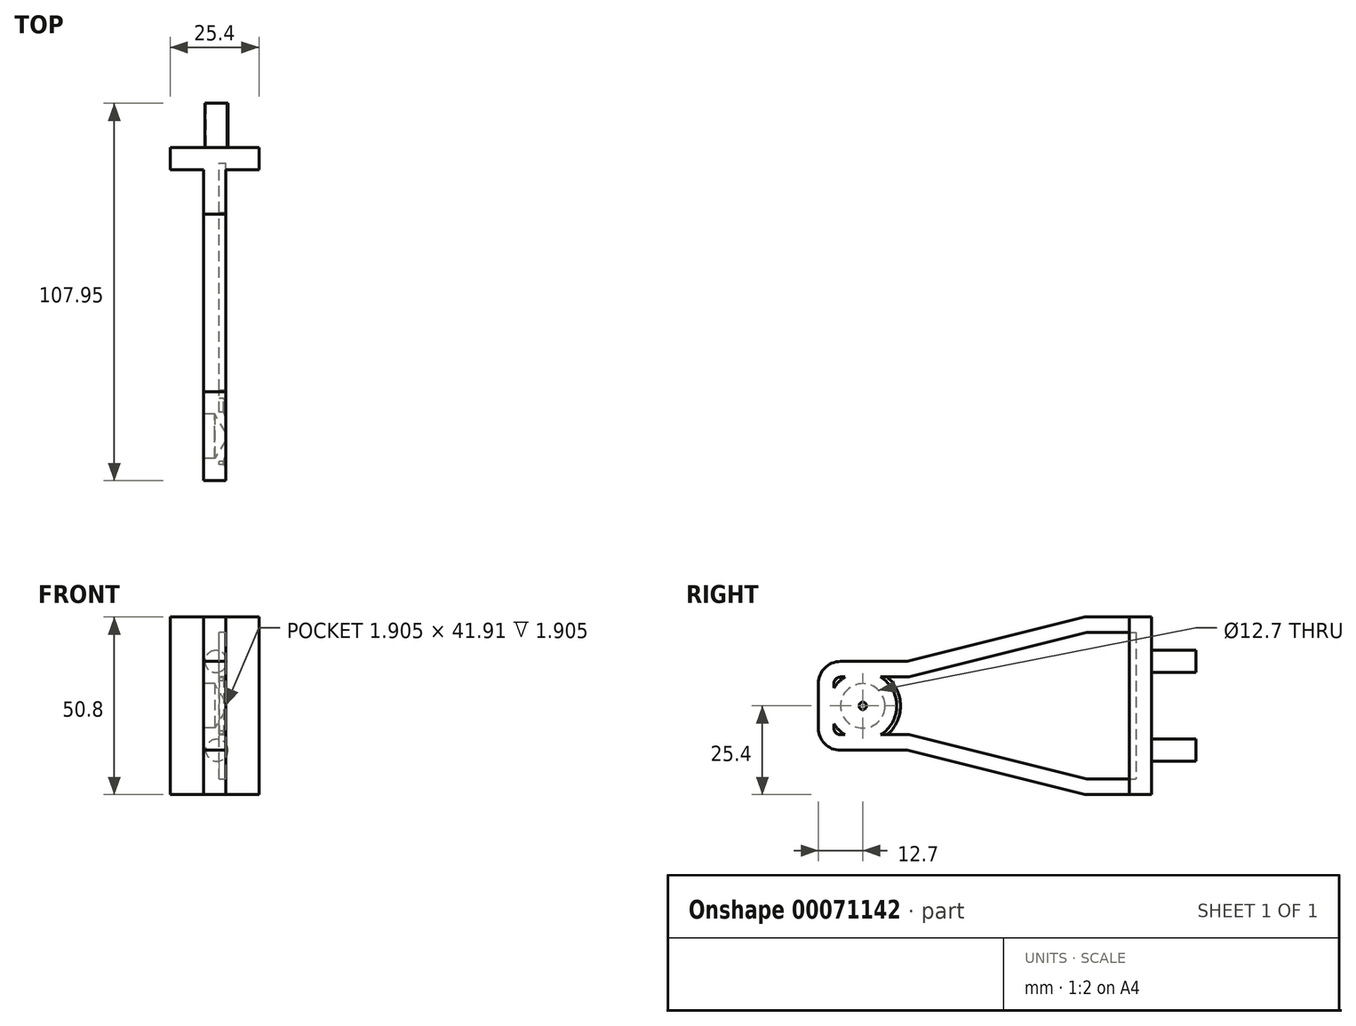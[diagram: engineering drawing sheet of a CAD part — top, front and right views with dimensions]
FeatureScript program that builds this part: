
annotation { "Feature Type Name" : "Feature", "Feature Type Description" : "" }
export const myFeature = defineFeature(function(context is Context, id is Id, definition is map)
    precondition{}
    {
        {
            var Q0;
            Q0=qCreatedBy(makeId("Front.planeOp"),FACE);
            var sketch = newSketch(context, id + "F0", { "sketchPlane" : qUnion([Q0])});
            skLineSegment(sketch, "E0.bottom", {"start": v(0, 0) * mm, "end": v(25.4, 0) * mm});
            skLineSegment(sketch, "E0.top", {"start": v(0, 50.8) * mm, "end": v(25.4, 50.8) * mm});
            skLineSegment(sketch, "E0.left", {"start": v(0, 0) * mm, "end": v(0, 50.8) * mm});
            skLineSegment(sketch, "E0.right", {"start": v(25.4, 0) * mm, "end": v(25.4, 50.8) * mm});
            skSolve(sketch);
        }
        {
            var Q0;
            Q0=makeQuery(id+"F0.imprint","IMPRINT",FACE,{"disambiguationData":[TD([[makeQuery(id+"F0.imprint","IMPRINT",EDGE,{"derivedFrom":sQuery(id+"F0.wireOp",EDGE,"E0.bottom")}),1.0]])]});
            extrude(context, id + "F1", {"entities" : qUnion([Q0]), "depth" : 6.35 * mm});
        }
        {
            var Q0;
            Q0=makeQuery(id+"F1.opExtrude","CAP_FACE",FACE,{"disambiguationData":[OSD([sQuery(id+"F0.wireOp",EDGE,"E0.bottom"),sQuery(id+"F0.wireOp",EDGE,"E0.top"),sQuery(id+"F0.wireOp",EDGE,"E0.left"),sQuery(id+"F0.wireOp",EDGE,"E0.right")])],"isStart":false});
            var sketch = newSketch(context, id + "F2", { "sketchPlane" : qUnion([Q0])});
            skLineSegment(sketch, "E1.bottom", {"start": v(9.53, 0) * mm, "end": v(15.88, 0) * mm});
            skLineSegment(sketch, "E1.top", {"start": v(9.53, 50.8) * mm, "end": v(15.88, 50.8) * mm});
            skLineSegment(sketch, "E1.left", {"start": v(9.53, 0) * mm, "end": v(9.53, 50.8) * mm});
            skLineSegment(sketch, "E1.right", {"start": v(15.88, 0) * mm, "end": v(15.88, 50.8) * mm});
            skSolve(sketch);
        }
        {
            var Q0;
            Q0=makeQuery(id+"F2.imprint","IMPRINT",FACE,{"disambiguationData":[TD([[makeQuery(id+"F2.imprint","IMPRINT",EDGE,{"derivedFrom":sQuery(id+"F2.wireOp",EDGE,"E1.bottom")}),1.0]])]});
            extrude(context, id + "F3", {"entities" : qUnion([Q0]), "operationType" : NewBodyOperationType.ADD, "depth" : 12.7 * mm});
        }
        {
            var Q0;
            Q0=makeQuery(id+"F3.opExtrude","CAP_FACE",FACE,{"disambiguationData":[OSD([sQuery(id+"F2.wireOp",EDGE,"E1.bottom"),sQuery(id+"F2.wireOp",EDGE,"E1.top"),sQuery(id+"F2.wireOp",EDGE,"E1.left"),sQuery(id+"F2.wireOp",EDGE,"E1.right")])],"isStart":false});
            cPlane(context, id + "F4", {"entities" : qUnion([Q0]), "cplaneType" : CPlaneType.OFFSET, "offset" : 50.8 * mm, "width" : 152.4 * mm, "height" : 152.4 * mm});
        }
        {
            var Q0;
            Q0=qCreatedBy(id+"F4.planeOp",FACE);
            var sketch = newSketch(context, id + "F5", { "sketchPlane" : qUnion([Q0])});
            skLineSegment(sketch, "E2.0", {"start": v(9.53, 12.7) * mm, "end": v(9.53, 38.1) * mm});
            skLineSegment(sketch, "E3.0", {"start": v(15.88, 12.7) * mm, "end": v(15.88, 38.1) * mm});
            skLineSegment(sketch, "E4", {"start": v(9.53, 12.7) * mm, "end": v(15.88, 12.7) * mm});
            skLineSegment(sketch, "E5", {"start": v(9.53, 38.1) * mm, "end": v(15.88, 38.1) * mm});
            skSolve(sketch);
        }
        {
            var Q1;
            Q1=makeQuery(id+"F3.opExtrude","CAP_FACE",FACE,{"disambiguationData":[OSD([sQuery(id+"F2.wireOp",EDGE,"E1.bottom"),sQuery(id+"F2.wireOp",EDGE,"E1.top"),sQuery(id+"F2.wireOp",EDGE,"E1.left"),sQuery(id+"F2.wireOp",EDGE,"E1.right")])],"isStart":false});
            var Q2;
            Q2=makeQuery(id+"F5.imprint","IMPRINT",FACE,{"disambiguationData":[TD([[makeQuery(id+"F5.imprint","IMPRINT",EDGE,{"derivedFrom":sQuery(id+"F5.wireOp",EDGE,"E2.0")}),-1.0]])]});
            loft(context, id + "F6", {"operationType" : NewBodyOperationType.ADD, "sheetProfilesArray" : [{ "sheetProfileEntities" : qUnion([Q1]) }, { "sheetProfileEntities" : qUnion([Q2]) }]});
        }
        {
            var Q0;
            Q0=makeQuery(id+"F6.opLoft","CAP_FACE",FACE,{"disambiguationData":[OSD([makeQuery(id+"F5.imprint","IMPRINT",FACE,{"disambiguationData":[TD([[makeQuery(id+"F5.imprint","IMPRINT",EDGE,{"derivedFrom":sQuery(id+"F5.wireOp",EDGE,"E2.0")}),-1.0]])]})])],"isStart":true});
            extrude(context, id + "F7", {"entities" : qUnion([Q0]), "operationType" : NewBodyOperationType.ADD, "depth" : 25.4 * mm});
        }
        {
            var Q0;
            Q0=makeQuery(id+"F7.opExtrude","CAP_EDGE",EDGE,{"disambiguationData":[OSD([sQuery(id+"F5.wireOp",EDGE,"E2.0"),sQuery(id+"F5.wireOp",EDGE,"E3.0"),sQuery(id+"F5.wireOp",EDGE,"E5")])],"isStart":false});
            var Q1;
            Q1=makeQuery(id+"F7.opExtrude","CAP_EDGE",EDGE,{"disambiguationData":[OSD([sQuery(id+"F5.wireOp",EDGE,"E2.0"),sQuery(id+"F5.wireOp",EDGE,"E3.0"),sQuery(id+"F5.wireOp",EDGE,"E4")])],"isStart":false});
            fillet(context, id + "F8", {"entities" : qUnion([Q0, Q1]), "radius" : 6.35 * mm, "tangentPropagation" : true, "allowEdgeOverflow" : false});
        }
        {
            var Q0;
            {var subQ0=sQuery(id+"F5.wireOp",EDGE,"E5");var subQ1=sQuery(id+"F5.wireOp",EDGE,"E4");var subQ2=sQuery(id+"F5.wireOp",EDGE,"E2.0");var subQ3=sQuery(id+"F2.wireOp",EDGE,"E1.left");Q0=makeQuery(id+"F7.boolean.opBoolean","MERGE",FACE,{"derivedFrom":[makeQuery(id+"F6.boolean.opBoolean","MERGE",FACE,{"derivedFrom":[makeQuery(id+"F3.opExtrude","SWEPT_FACE",FACE,{"disambiguationData":[OSD([subQ3])]}),makeQuery(id+"F6.opLoft","SWEPT_FACE",FACE,{"disambiguationData":[OSD([sQuery(id+"F0.wireOp",EDGE,"E0.bottom"),sQuery(id+"F0.wireOp",EDGE,"E0.top"),sQuery(id+"F2.wireOp",EDGE,"E1.bottom"),sQuery(id+"F2.wireOp",EDGE,"E1.top"),subQ3,subQ2,subQ1,subQ0])]})]}),makeQuery(id+"F7.opExtrude","SWEPT_FACE",FACE,{"disambiguationData":[OSD([subQ2,subQ1,subQ0])]})]});}
            var sketch = newSketch(context, id + "F9", { "sketchPlane" : qUnion([Q0])});
            skPoint(sketch, "E6", {"position": v(82.55, 25.4) * mm});
            skPoint(sketch, "E6.positionSnap0", {"position": v(95.25, 25.4) * mm});
            skSolve(sketch);
        }
        {
            var Q0;
            Q0=sQuery(id+"F9.wireOp",VERTEX,"E6");
            var Q1;
            Q1=makeQuery(id+"F1.opExtrude","SWEPT_BODY",BODY,{"disambiguationData":[OSD([sQuery(id+"F0.wireOp",EDGE,"E0.bottom"),sQuery(id+"F0.wireOp",EDGE,"E0.top"),sQuery(id+"F0.wireOp",EDGE,"E0.left"),sQuery(id+"F0.wireOp",EDGE,"E0.right")])]});
            hole(context, id + "F10", {"style" : HoleStyle.SIMPLE, "holeDiameter" : 12.7 * mm, "endStyle" : HoleEndStyle.BLIND, "holeDepth" : 3.17 * mm, "locations" : qUnion([Q0]), "scope" : qUnion([Q1])});
        }
        {
            var Q0;
            Q0=makeQuery(id+"F1.opExtrude","CAP_FACE",FACE,{"disambiguationData":[OSD([sQuery(id+"F0.wireOp",EDGE,"E0.bottom"),sQuery(id+"F0.wireOp",EDGE,"E0.top"),sQuery(id+"F0.wireOp",EDGE,"E0.left"),sQuery(id+"F0.wireOp",EDGE,"E0.right")])],"isStart":true});
            var sketch = newSketch(context, id + "F11", { "sketchPlane" : qUnion([Q0])});
            skCircle(sketch, "E7", {"center": v(-13.35, 12.7) * mm, "radius": 3.18 * mm});
            skCircle(sketch, "E8", {"center": v(-13.07, 38.1) * mm, "radius": 3.18 * mm});
            skSolve(sketch);
        }
        {
            var Q0;
            Q0 = qSketchRegion(id + "F11", true);
            extrude(context, id + "F12", {"entities" : qUnion([Q0]), "operationType" : NewBodyOperationType.ADD, "depth" : 12.7 * mm});
        }
        {
            var Q0;
            {var subQ0=sQuery(id+"F5.wireOp",EDGE,"E5");var subQ1=sQuery(id+"F5.wireOp",EDGE,"E4");var subQ2=sQuery(id+"F5.wireOp",EDGE,"E3.0");var subQ3=sQuery(id+"F2.wireOp",EDGE,"E1.right");Q0=makeQuery(id+"F7.boolean.opBoolean","MERGE",FACE,{"derivedFrom":[makeQuery(id+"F6.boolean.opBoolean","MERGE",FACE,{"derivedFrom":[makeQuery(id+"F3.opExtrude","SWEPT_FACE",FACE,{"disambiguationData":[OSD([subQ3])]}),makeQuery(id+"F6.opLoft","SWEPT_FACE",FACE,{"disambiguationData":[OSD([sQuery(id+"F0.wireOp",EDGE,"E0.bottom"),sQuery(id+"F0.wireOp",EDGE,"E0.top"),sQuery(id+"F2.wireOp",EDGE,"E1.bottom"),sQuery(id+"F2.wireOp",EDGE,"E1.top"),subQ3,subQ2,subQ1,subQ0])]})]}),makeQuery(id+"F7.opExtrude","SWEPT_FACE",FACE,{"disambiguationData":[OSD([subQ2,subQ1,subQ0])]})]});}
            shell(context, id + "F13", {"entities" : qUnion([Q0]), "thickness" : 4.44 * mm});
        }
    });
